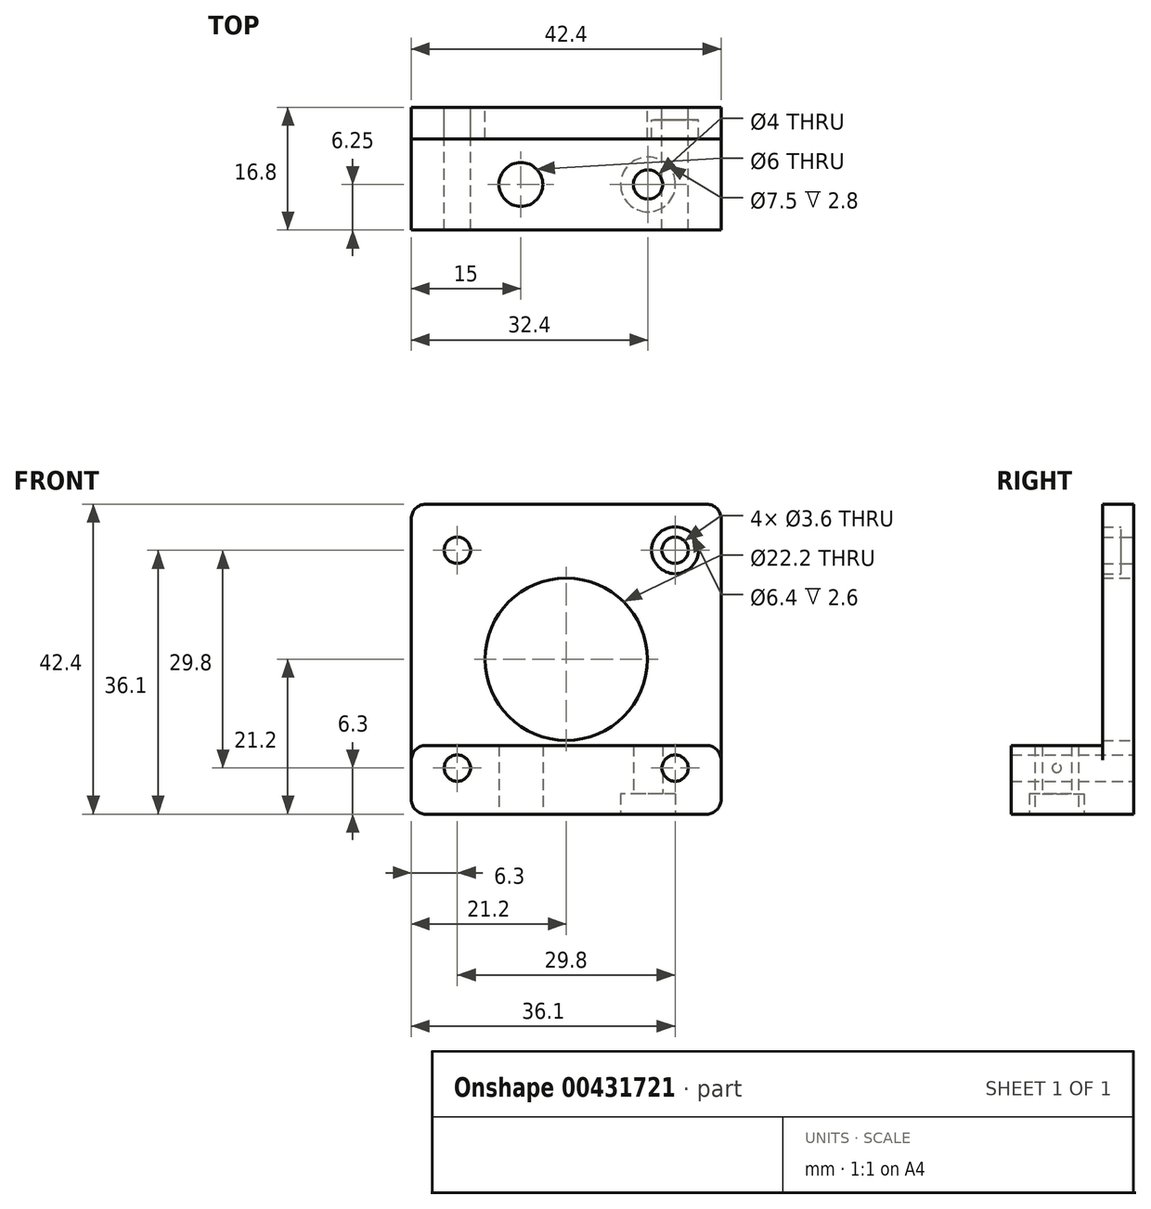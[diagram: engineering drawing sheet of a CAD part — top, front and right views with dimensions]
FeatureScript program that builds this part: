
annotation { "Feature Type Name" : "Feature", "Feature Type Description" : "" }
export const myFeature = defineFeature(function(context is Context, id is Id, definition is map)
    precondition{}
    {
        {
            var Q0;
            Q0=qCreatedBy(makeId("Front.planeOp"),FACE);
            var sketch = newSketch(context, id + "F0", { "sketchPlane" : qUnion([Q0])});
            skLineSegment(sketch, "E0.bottom", {"start": v(-19.2, 21.2) * mm, "end": v(19.2, 21.2) * mm});
            skLineSegment(sketch, "E0.top", {"start": v(-19.2, -21.2) * mm, "end": v(19.2, -21.2) * mm});
            skLineSegment(sketch, "E0.left", {"start": v(-21.2, 19.2) * mm, "end": v(-21.2, -19.2) * mm});
            skLineSegment(sketch, "E0.right", {"start": v(21.2, 19.2) * mm, "end": v(21.2, -19.2) * mm});
            skPoint(sketch, "E0.middle", {"position": v(0, 0) * mm});
            skCircle(sketch, "E1", {"center": v(0, 0) * mm, "radius": 11.1 * mm});
            skArc(sketch, "E2.filletArc", {"start": v(-19.2, 21.2) * mm, "mid": v(-20.61, 20.61) * mm, "end": v(-21.2, 19.2) * mm});
            skArc(sketch, "E3.filletArc", {"start": v(21.2, 19.2) * mm, "mid": v(20.61, 20.61) * mm, "end": v(19.2, 21.2) * mm});
            skArc(sketch, "E4.filletArc", {"start": v(19.2, -21.2) * mm, "mid": v(20.61, -20.61) * mm, "end": v(21.2, -19.2) * mm});
            skArc(sketch, "E5.filletArc", {"start": v(-21.2, -19.2) * mm, "mid": v(-20.61, -20.61) * mm, "end": v(-19.2, -21.2) * mm});
            skCircle(sketch, "E6", {"center": v(-14.9, 14.9) * mm, "radius": 1.8 * mm});
            skCircle(sketch, "E7", {"center": v(14.9, 14.9) * mm, "radius": 1.8 * mm});
            skCircle(sketch, "E8", {"center": v(-14.9, -14.9) * mm, "radius": 1.8 * mm});
            skCircle(sketch, "E9", {"center": v(14.9, -14.9) * mm, "radius": 1.8 * mm});
            skLineSegment(sketch, "E10", {"start": v(-19.2, -11.8) * mm, "end": v(19.2, -11.8) * mm});
            skArc(sketch, "E11", {"start": v(-19.2, -11.8) * mm, "mid": v(-20.61, -12.39) * mm, "end": v(-21.2, -13.8) * mm});
            skArc(sketch, "E12", {"start": v(21.2, -13.8) * mm, "mid": v(20.61, -12.39) * mm, "end": v(19.2, -11.8) * mm});
            skLineSegment(sketch, "E13", {"start": v(-19.2, 19.2) * mm, "end": v(-14.9, 14.9) * mm, "construction": true});
            skLineSegment(sketch, "E14", {"start": v(14.9, 14.9) * mm, "end": v(19.2, 19.2) * mm, "construction": true});
            skLineSegment(sketch, "E15", {"start": v(14.9, -14.9) * mm, "end": v(19.2, -19.2) * mm, "construction": true});
            skLineSegment(sketch, "E16", {"start": v(-14.9, -14.9) * mm, "end": v(-19.2, -19.2) * mm, "construction": true});
            skLineSegment(sketch, "E17.left", {"start": v(-9.2, -11.8) * mm, "end": v(-9.2, -21.2) * mm, "construction": true});
            skLineSegment(sketch, "E17.right", {"start": v(-3.2, -11.8) * mm, "end": v(-3.2, -21.2) * mm, "construction": true});
            skLineSegment(sketch, "E18", {"start": v(-6.2, -11.8) * mm, "end": v(-6.2, -21.2) * mm, "construction": true});
            skCircle(sketch, "E19", {"center": v(14.9, 14.9) * mm, "radius": 3.2 * mm});
            skLineSegment(sketch, "E20", {"start": v(11.2, -11.8) * mm, "end": v(11.2, -21.2) * mm, "construction": true});
            skLineSegment(sketch, "E21", {"start": v(9.2, -11.8) * mm, "end": v(9.2, -18.4) * mm, "construction": true});
            skLineSegment(sketch, "E22", {"start": v(13.2, -11.8) * mm, "end": v(13.2, -18.4) * mm, "construction": true});
            skLineSegment(sketch, "E23", {"start": v(7.45, -18.4) * mm, "end": v(14.95, -18.4) * mm, "construction": true});
            skLineSegment(sketch, "E24", {"start": v(7.45, -18.4) * mm, "end": v(7.45, -21.2) * mm, "construction": true});
            skLineSegment(sketch, "E25", {"start": v(14.95, -18.4) * mm, "end": v(14.95, -21.2) * mm, "construction": true});
            skSolve(sketch);
        }
        {
            var Q0;
            Q0=qCreatedBy(makeId("Right.planeOp"),FACE);
            var sketch = newSketch(context, id + "F1", { "sketchPlane" : qUnion([Q0])});
            skLineSegment(sketch, "E26.bottom", {"start": v(-4.3, 21.2) * mm, "end": v(0, 21.2) * mm});
            skLineSegment(sketch, "E26.left", {"start": v(-4.3, 21.2) * mm, "end": v(-4.3, -11.8) * mm});
            skLineSegment(sketch, "E27.bottom", {"start": v(-16.8, -11.8) * mm, "end": v(-4.3, -11.8) * mm});
            skLineSegment(sketch, "E27.top", {"start": v(-16.8, -21.2) * mm, "end": v(0, -21.2) * mm});
            skLineSegment(sketch, "E27.left", {"start": v(-16.8, -11.8) * mm, "end": v(-16.8, -21.2) * mm});
            skLineSegment(sketch, "E28", {"start": v(-4.3, 14.9) * mm, "end": v(0, 14.9) * mm, "construction": true});
            skLineSegment(sketch, "E29", {"start": v(-16.8, -14.9) * mm, "end": v(0, -14.9) * mm, "construction": true});
            skLineSegment(sketch, "E30", {"start": v(-10.55, -11.8) * mm, "end": v(-10.55, -21.2) * mm, "construction": true});
            skLineSegment(sketch, "E31", {"start": v(0, 21.2) * mm, "end": v(0, -21.2) * mm});
            skLineSegment(sketch, "E32", {"start": v(0, 16.7) * mm, "end": v(-1.7, 16.7) * mm, "construction": true});
            skLineSegment(sketch, "E33", {"start": v(0, 13.1) * mm, "end": v(-1.7, 13.1) * mm, "construction": true});
            skLineSegment(sketch, "E34", {"start": v(-1.7, 11.7) * mm, "end": v(-1.7, 18.1) * mm, "construction": true});
            skLineSegment(sketch, "E35", {"start": v(-1.7, 18.1) * mm, "end": v(-4.3, 18.1) * mm, "construction": true});
            skLineSegment(sketch, "E36", {"start": v(-1.7, 11.7) * mm, "end": v(-4.3, 11.7) * mm, "construction": true});
            skLineSegment(sketch, "E37.0", {"start": v(0, 13.1) * mm, "end": v(0, 16.7) * mm, "construction": true});
            skLineSegment(sketch, "E38.0", {"start": v(0, 11.7) * mm, "end": v(0, 18.1) * mm, "construction": true});
            skSolve(sketch);
        }
        {
            var Q0;
            Q0=makeQuery(id+"F0.imprint","IMPRINT",FACE,{"disambiguationData":[TD([[makeQuery(id+"F0.imprint","IMPRINT",EDGE,{"derivedFrom":sQuery(id+"F0.wireOp",EDGE,"E0.top")}),1.0]])]});
            var Q1;
            Q1=makeQuery(id+"F0.imprint","IMPRINT",FACE,{"disambiguationData":[TD([[makeQuery(id+"F0.imprint","IMPRINT",EDGE,{"derivedFrom":sQuery(id+"F0.wireOp",EDGE,"E0.bottom")}),-1.0]])]});
            var Q2;
            Q2=sQuery(id+"F1.wireOp",VERTEX,"E26.left.start");
            extrude(context, id + "F2", {"entities" : qUnion([Q0, Q1]), "endBound" : BoundingType.UP_TO_VERTEX, "endBoundEntityVertex" : qUnion([Q2]), "depth" : 25 * mm});
        }
        {
            var Q0;
            Q0=makeQuery(id+"F0.imprint","IMPRINT",FACE,{"disambiguationData":[TD([[makeQuery(id+"F0.imprint","IMPRINT",EDGE,{"derivedFrom":sQuery(id+"F0.wireOp",EDGE,"E7")}),-1.0]])]});
            var Q1;
            Q1=sQuery(id+"F1.wireOp",VERTEX,"E33.end");
            extrude(context, id + "F3", {"entities" : qUnion([Q0]), "operationType" : NewBodyOperationType.ADD, "endBound" : BoundingType.UP_TO_VERTEX, "endBoundEntityVertex" : qUnion([Q1]), "depth" : 25 * mm});
        }
        {
            var Q0;
            Q0=makeQuery(id+"F0.imprint","IMPRINT",FACE,{"disambiguationData":[TD([[makeQuery(id+"F0.imprint","IMPRINT",EDGE,{"derivedFrom":sQuery(id+"F0.wireOp",EDGE,"E0.top")}),1.0]])]});
            var Q1;
            Q1=sQuery(id+"F1.wireOp",VERTEX,"E27.left.start");
            extrude(context, id + "F4", {"entities" : qUnion([Q0]), "operationType" : NewBodyOperationType.ADD, "endBound" : BoundingType.UP_TO_VERTEX, "endBoundEntityVertex" : qUnion([Q1]), "depth" : 25 * mm});
        }
        {
            var Q0;
            {var subQ0=sQuery(id+"F0.wireOp",EDGE,"E0.top");Q0=makeQuery(id+"F4.boolean.opBoolean","MERGE",FACE,{"derivedFrom":[makeQuery(id+"F2.opExtrude","SWEPT_FACE",FACE,{"disambiguationData":[OSD([subQ0])]}),makeQuery(id+"F4.opExtrude","SWEPT_FACE",FACE,{"disambiguationData":[OSD([subQ0])]})]});}
            var sketch = newSketch(context, id + "F5", { "sketchPlane" : qUnion([Q0])});
            skLineSegment(sketch, "E39", {"start": v(-6.2, 0) * mm, "end": v(-6.2, 16.8) * mm, "construction": true});
            skLineSegment(sketch, "E40", {"start": v(11.2, 0) * mm, "end": v(11.2, 16.8) * mm, "construction": true});
            skLineSegment(sketch, "E41", {"start": v(-19.2, 10.55) * mm, "end": v(19.2, 10.55) * mm, "construction": true});
            skCircle(sketch, "E42", {"center": v(11.2, 10.55) * mm, "radius": 2 * mm});
            skCircle(sketch, "E43", {"center": v(11.2, 10.55) * mm, "radius": 3.75 * mm});
            skLineSegment(sketch, "E44", {"start": v(-9.2, 0) * mm, "end": v(-9.2, 16.8) * mm, "construction": true});
            skCircle(sketch, "E45", {"center": v(-6.2, 10.55) * mm, "radius": 3 * mm});
            skLineSegment(sketch, "E46", {"start": v(7.45, 0) * mm, "end": v(7.45, 16.8) * mm, "construction": true});
            skLineSegment(sketch, "E47", {"start": v(9.2, 0) * mm, "end": v(9.2, 16.8) * mm, "construction": true});
            skSolve(sketch);
        }
        {
            var Q0;
            Q0=makeQuery(id+"F5.imprint","IMPRINT",FACE,{"disambiguationData":[TD([[makeQuery(id+"F5.imprint","IMPRINT",EDGE,{"derivedFrom":sQuery(id+"F5.wireOp",EDGE,"E45")}),1.0]])]});
            var Q1;
            Q1=makeQuery(id+"F5.imprint","IMPRINT",FACE,{"disambiguationData":[TD([[makeQuery(id+"F5.imprint","IMPRINT",EDGE,{"derivedFrom":sQuery(id+"F5.wireOp",EDGE,"E42")}),1.0]])]});
            extrude(context, id + "F6", {"entities" : qUnion([Q0, Q1]), "operationType" : NewBodyOperationType.REMOVE, "endBound" : BoundingType.THROUGH_ALL, "oppositeDirection" : true, "depth" : 25 * mm});
        }
        {
            var Q0;
            Q0=makeQuery(id+"F5.imprint","IMPRINT",FACE,{"disambiguationData":[TD([[makeQuery(id+"F5.imprint","IMPRINT",EDGE,{"derivedFrom":sQuery(id+"F5.wireOp",EDGE,"E42")}),-1.0]])]});
            var Q1;
            Q1=sQuery(id+"F0.wireOp",VERTEX,"E24.start");
            extrude(context, id + "F7", {"entities" : qUnion([Q0]), "operationType" : NewBodyOperationType.REMOVE, "endBound" : BoundingType.UP_TO_VERTEX, "oppositeDirection" : true, "endBoundEntityVertex" : qUnion([Q1]), "depth" : 25 * mm});
        }
    });
